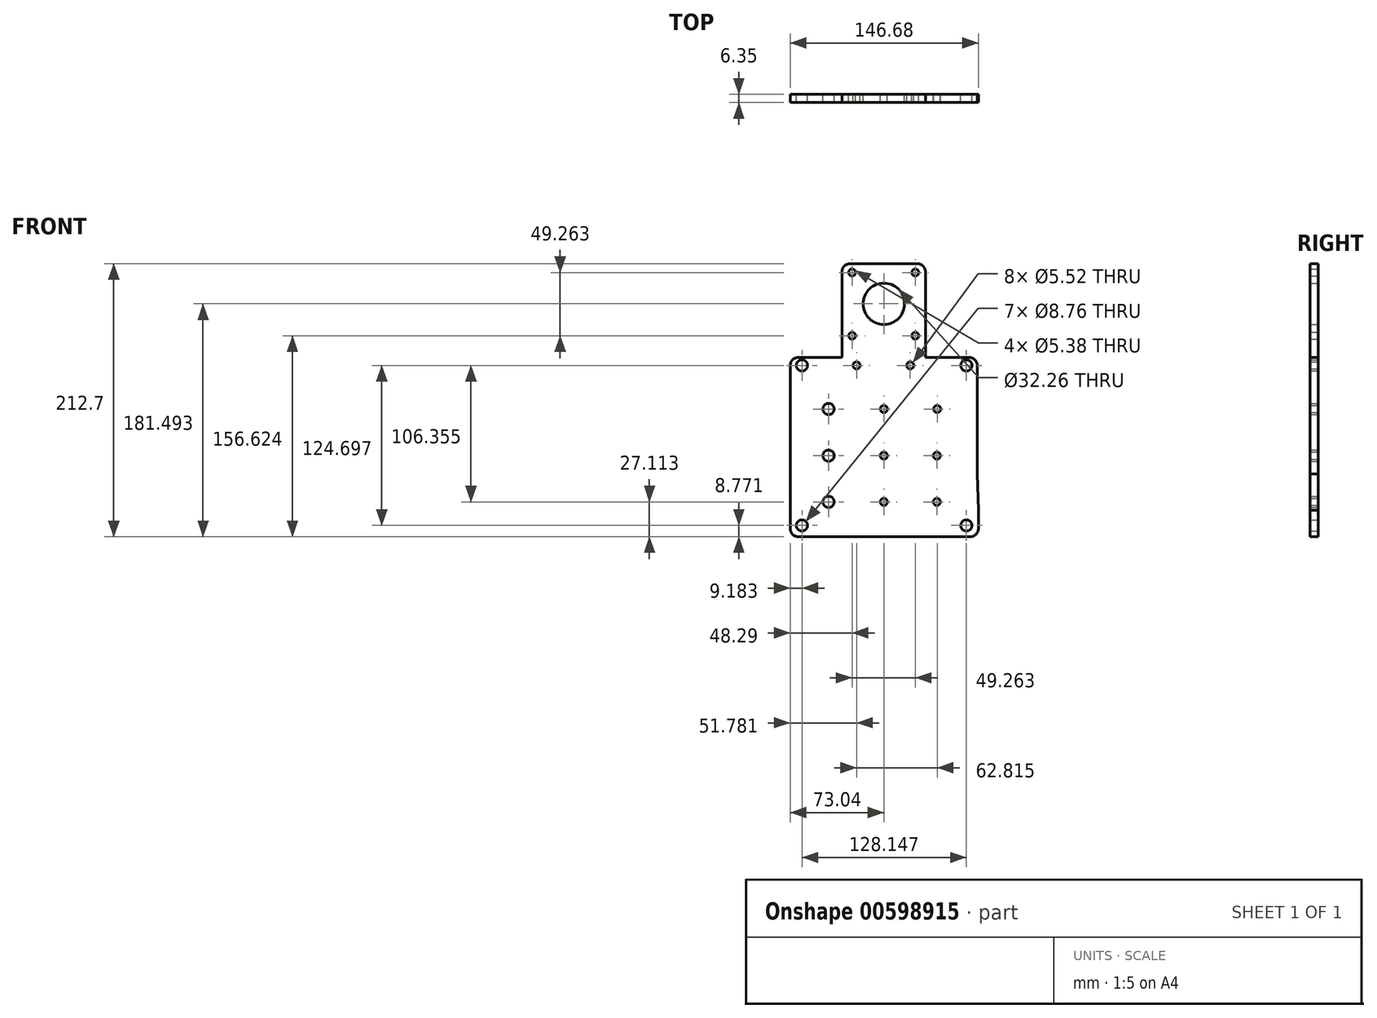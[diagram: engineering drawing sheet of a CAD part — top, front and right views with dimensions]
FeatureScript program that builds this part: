
annotation { "Feature Type Name" : "Feature", "Feature Type Description" : "" }
export const myFeature = defineFeature(function(context is Context, id is Id, definition is map)
    precondition{}
    {
        {
            var Q0;
            Q0=qCreatedBy(makeId("Front.planeOp"),FACE);
            var sketch = newSketch(context, id + "F0", { "sketchPlane" : qUnion([Q0])});
            skLineSegment(sketch, "E0.bottom", {"start": v(66.45, 76.55) * mm, "end": v(-66.69, 76.55) * mm});
            skLineSegment(sketch, "E0.top", {"start": v(67.3, -63.15) * mm, "end": v(-66.69, -63.15) * mm});
            skPoint(sketch, "E0.middle", {"position": v(0, 0) * mm});
            skLineSegment(sketch, "E1", {"start": v(73.64, -56.8) * mm, "end": v(73.64, -42.59) * mm});
            skLineSegment(sketch, "E2", {"start": v(-73.04, -56.8) * mm, "end": v(-73.04, -42.6) * mm});
            skCircle(sketch, "E3", {"center": v(-63.86, 70.32) * mm, "radius": 4.38 * mm});
            skCircle(sketch, "E4", {"center": v(64.3, 70.32) * mm, "radius": 4.38 * mm});
            skCircle(sketch, "E5", {"center": v(-63.86, -54.38) * mm, "radius": 4.38 * mm});
            skCircle(sketch, "E6", {"center": v(64.3, -54.38) * mm, "radius": 4.38 * mm});
            skLineSegment(sketch, "E7", {"start": v(72.8, -14.15) * mm, "end": v(73.64, -42.59) * mm});
            skCircle(sketch, "E8", {"center": v(0, 36.33) * mm, "radius": 2.76 * mm});
            skCircle(sketch, "E9", {"center": v(0, 0) * mm, "radius": 2.76 * mm});
            skCircle(sketch, "E10", {"center": v(0, -36.04) * mm, "radius": 2.76 * mm});
            skCircle(sketch, "E11", {"center": v(-43.13, 36.33) * mm, "radius": 4.38 * mm});
            skCircle(sketch, "E12", {"center": v(-43.13, 0) * mm, "radius": 4.38 * mm});
            skCircle(sketch, "E13", {"center": v(-43.13, -36.04) * mm, "radius": 4.38 * mm});
            skLineSegment(sketch, "E14", {"start": v(-32.71, 76.55) * mm, "end": v(-32.71, 143.2) * mm});
            skLineSegment(sketch, "E15", {"start": v(-26.36, 149.55) * mm, "end": v(26.11, 149.55) * mm});
            skCircle(sketch, "E16", {"center": v(-24.75, 142.74) * mm, "radius": 2.69 * mm});
            skCircle(sketch, "E17", {"center": v(24.51, 142.74) * mm, "radius": 2.69 * mm});
            skCircle(sketch, "E18", {"center": v(24.51, 93.47) * mm, "radius": 2.69 * mm});
            skCircle(sketch, "E19", {"center": v(-24.75, 93.47) * mm, "radius": 2.69 * mm});
            skLineSegment(sketch, "E20", {"start": v(32.46, 143.2) * mm, "end": v(32.46, 76.55) * mm});
            skCircle(sketch, "E21", {"center": v(41.56, 36.33) * mm, "radius": 2.76 * mm});
            skCircle(sketch, "E22", {"center": v(41.31, 0) * mm, "radius": 2.76 * mm});
            skCircle(sketch, "E23", {"center": v(41.31, -36.04) * mm, "radius": 2.76 * mm});
            skCircle(sketch, "E24", {"center": v(-21.26, 70.32) * mm, "radius": 2.76 * mm});
            skCircle(sketch, "E25", {"center": v(20.53, 70.32) * mm, "radius": 2.76 * mm});
            skLineSegment(sketch, "E26", {"start": v(-73.04, 70.2) * mm, "end": v(-73.04, -14.15) * mm});
            skLineSegment(sketch, "E27", {"start": v(72.8, 70.2) * mm, "end": v(72.8, -14.15) * mm});
            skLineSegment(sketch, "E28", {"start": v(-73.04, -14.15) * mm, "end": v(-73.04, -42.6) * mm});
            skCircle(sketch, "E29", {"center": v(0, 118.34) * mm, "radius": 16.13 * mm});
            skPoint(sketch, "E30.visualSharp", {"position": v(-32.71, 149.55) * mm});
            skArc(sketch, "E30.filletArc", {"start": v(-26.36, 149.55) * mm, "mid": v(-30.85, 147.69) * mm, "end": v(-32.71, 143.2) * mm});
            skPoint(sketch, "E31.visualSharp", {"position": v(32.46, 149.55) * mm});
            skArc(sketch, "E31.filletArc", {"start": v(32.46, 143.2) * mm, "mid": v(30.6, 147.69) * mm, "end": v(26.11, 149.55) * mm});
            skPoint(sketch, "E32.visualSharp", {"position": v(-73.04, 76.55) * mm});
            skArc(sketch, "E32.filletArc", {"start": v(-66.69, 76.55) * mm, "mid": v(-71.18, 74.7) * mm, "end": v(-73.04, 70.2) * mm});
            skPoint(sketch, "E33.visualSharp", {"position": v(72.8, 76.55) * mm});
            skArc(sketch, "E33.filletArc", {"start": v(72.8, 70.2) * mm, "mid": v(70.94, 74.7) * mm, "end": v(66.45, 76.55) * mm});
            skPoint(sketch, "E34.visualSharp", {"position": v(-73.04, -63.15) * mm});
            skArc(sketch, "E34.filletArc", {"start": v(-73.04, -56.8) * mm, "mid": v(-71.18, -61.29) * mm, "end": v(-66.69, -63.15) * mm});
            skPoint(sketch, "E35.visualSharp", {"position": v(73.64, -63.15) * mm});
            skArc(sketch, "E35.filletArc", {"start": v(67.3, -63.15) * mm, "mid": v(71.78, -61.29) * mm, "end": v(73.64, -56.8) * mm});
            skPoint(sketch, "E36.middle", {"position": v(0, 58.92) * mm});
            skSolve(sketch);
        }
        {
            var Q0;
            Q0=makeQuery(id+"F0.imprint","IMPRINT",FACE,{"disambiguationData":[TD([[makeQuery(id+"F0.imprint","IMPRINT",EDGE,{"derivedFrom":sQuery(id+"F0.wireOp",EDGE,"E0.top")}),-1.0]])]});
            var Q1;
            {var subQ1=sQuery(id+"F0.wireOp",EDGE,"E14");Q1=makeQuery(id+"F0.imprint","IMPRINT",FACE,{"disambiguationData":[TD([[makeQuery(id+"F0.imprint","IMPRINT",EDGE,{"derivedFrom":subQ1}),-1.0]])]});}
            extrude(context, id + "F1", {"entities" : qUnion([Q0, Q1]), "depth" : 6.35 * mm, "offsetDistance" : 25.4 * mm});
        }
    });
